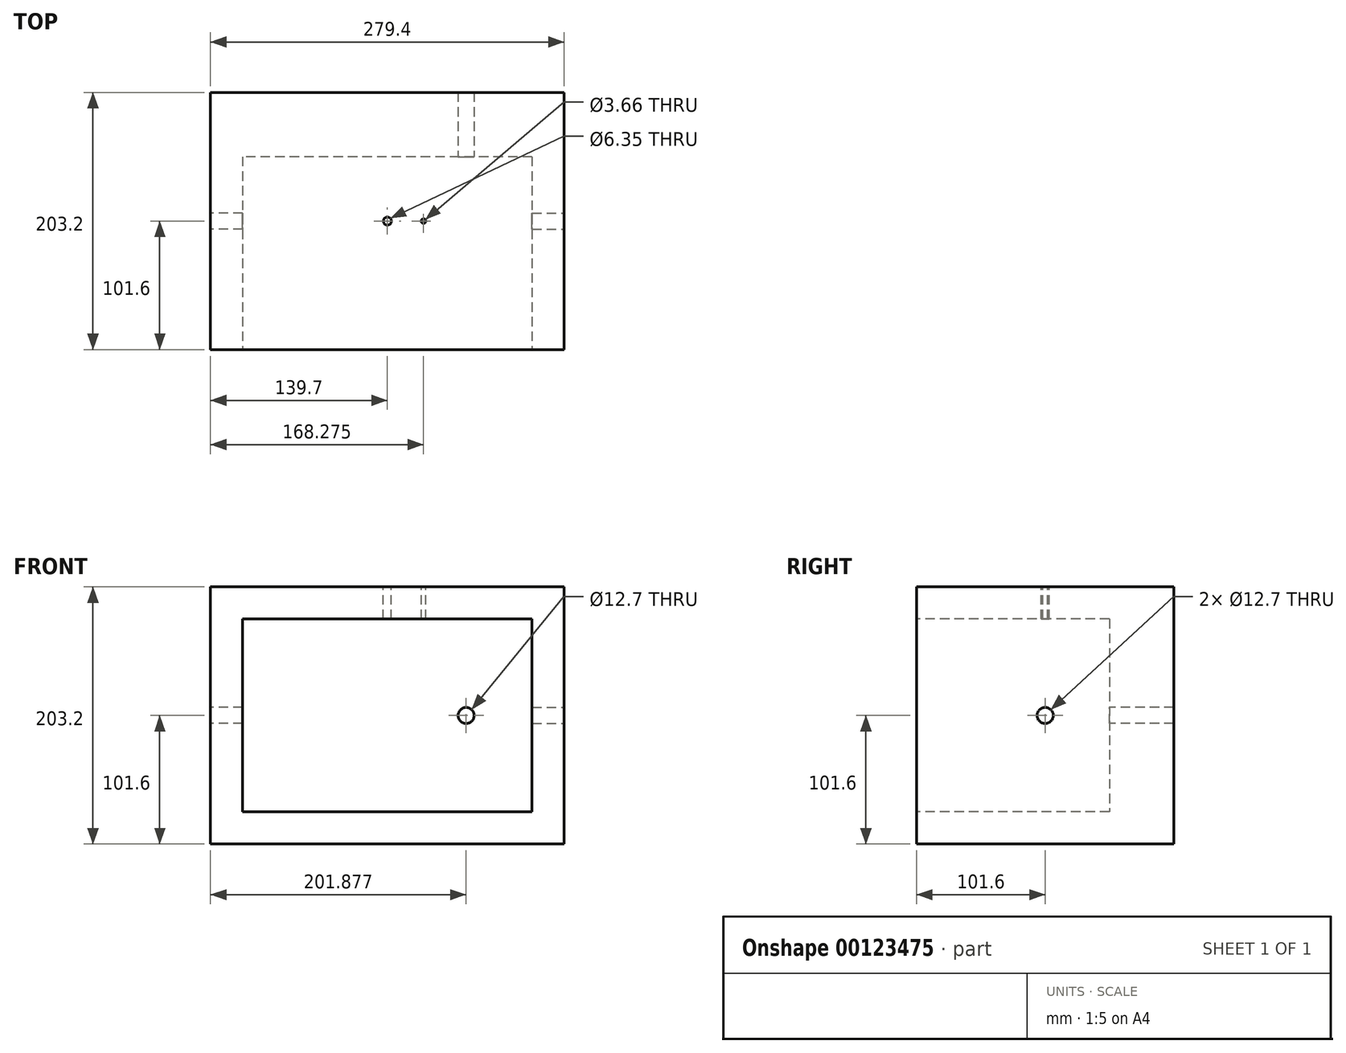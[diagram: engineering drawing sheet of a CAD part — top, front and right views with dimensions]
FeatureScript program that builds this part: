
annotation { "Feature Type Name" : "Feature", "Feature Type Description" : "" }
export const myFeature = defineFeature(function(context is Context, id is Id, definition is map)
    precondition{}
    {
        {
            var Q0;
            Q0=qCreatedBy(makeId("Front.planeOp"),FACE);
            var sketch = newSketch(context, id + "F0", { "sketchPlane" : qUnion([Q0])});
            skLineSegment(sketch, "E0.bottom", {"start": v(-139.7, 101.6) * mm, "end": v(139.7, 101.6) * mm});
            skLineSegment(sketch, "E0.top", {"start": v(-139.7, -101.6) * mm, "end": v(139.7, -101.6) * mm});
            skLineSegment(sketch, "E0.left", {"start": v(-139.7, 101.6) * mm, "end": v(-139.7, -101.6) * mm});
            skLineSegment(sketch, "E0.right", {"start": v(139.7, 101.6) * mm, "end": v(139.7, -101.6) * mm});
            skPoint(sketch, "E0.middle", {"position": v(0, 0) * mm});
            skSolve(sketch);
        }
        {
            var Q0;
            Q0=makeQuery(id+"F0.imprint","IMPRINT",FACE,{"disambiguationData":[TD([[makeQuery(id+"F0.imprint","IMPRINT",EDGE,{"derivedFrom":sQuery(id+"F0.wireOp",EDGE,"E0.bottom")}),-1.0]])]});
            extrude(context, id + "F1", {"entities" : qUnion([Q0]), "oppositeDirection" : true, "depth" : 203.2 * mm});
        }
        {
            var Q0;
            Q0=makeQuery(id+"F1.opExtrude","SWEPT_FACE",FACE,{"disambiguationData":[OSD([sQuery(id+"F0.wireOp",EDGE,"E0.bottom")])]});
            var sketch = newSketch(context, id + "F2", { "sketchPlane" : qUnion([Q0])});
            skCircle(sketch, "E1", {"center": v(0, 101.6) * mm, "radius": 3.18 * mm});
            skPoint(sketch, "E1.centerSnap0", {"position": v(139.7, 101.6) * mm});
            skLineSegment(sketch, "E2", {"start": v(0, 101.6) * mm, "end": v(28.58, 101.6) * mm, "construction": true});
            skCircle(sketch, "E3", {"center": v(28.58, 101.6) * mm, "radius": 1.83 * mm});
            skSolve(sketch);
        }
        {
            var Q0;
            Q0=makeQuery(id+"F1.opExtrude","SWEPT_FACE",FACE,{"disambiguationData":[OSD([sQuery(id+"F0.wireOp",EDGE,"E0.right")])]});
            var sketch = newSketch(context, id + "F3", { "sketchPlane" : qUnion([Q0])});
            skCircle(sketch, "E4", {"center": v(101.6, 0) * mm, "radius": 6.35 * mm});
            skPoint(sketch, "E4.centerSnap0", {"position": v(101.6, -101.6) * mm});
            skSolve(sketch);
        }
        {
            var Q0;
            Q0=makeQuery(id+"F1.opExtrude","SWEPT_FACE",FACE,{"disambiguationData":[OSD([sQuery(id+"F0.wireOp",EDGE,"E0.left")])]});
            var sketch = newSketch(context, id + "F4", { "sketchPlane" : qUnion([Q0])});
            skCircle(sketch, "E5", {"center": v(-101.6, 0) * mm, "radius": 6.35 * mm});
            skPoint(sketch, "E5.centerSnap0", {"position": v(-101.6, 101.6) * mm});
            skSolve(sketch);
        }
        {
            var Q0;
            Q0=qCreatedBy(makeId("Front.planeOp"),FACE);
            var sketch = newSketch(context, id + "F5", { "sketchPlane" : qUnion([Q0])});
            skLineSegment(sketch, "E6.bottom", {"start": v(114.3, 76.2) * mm, "end": v(-114.3, 76.2) * mm});
            skLineSegment(sketch, "E6.top", {"start": v(114.3, -76.2) * mm, "end": v(-114.3, -76.2) * mm});
            skLineSegment(sketch, "E6.left", {"start": v(114.3, 76.2) * mm, "end": v(114.3, -76.2) * mm});
            skLineSegment(sketch, "E6.right", {"start": v(-114.3, 76.2) * mm, "end": v(-114.3, -76.2) * mm});
            skSolve(sketch);
        }
        {
            var Q0;
            Q0=qSketchRegion(id+"F5",true);
            extrude(context, id + "F6", {"entities" : qUnion([Q0]), "operationType" : NewBodyOperationType.REMOVE, "oppositeDirection" : true, "depth" : 152.4 * mm});
        }
        {
            var Q0;
            Q0=makeQuery(id+"F2.imprint","IMPRINT",FACE,{"disambiguationData":[TD([[makeQuery(id+"F2.imprint","IMPRINT",EDGE,{"derivedFrom":sQuery(id+"F2.wireOp",EDGE,"E1")}),1.0]])]});
            var Q1;
            Q1=makeQuery(id+"F2.imprint","IMPRINT",FACE,{"disambiguationData":[TD([[makeQuery(id+"F2.imprint","IMPRINT",EDGE,{"derivedFrom":sQuery(id+"F2.wireOp",EDGE,"E3")}),1.0]])]});
            var Q2;
            Q2=sQuery(id+"F2.wireOp",EDGE,"E1");
            extrude(context, id + "F7", {"entities" : qUnion([Q0, Q1]), "operationType" : NewBodyOperationType.REMOVE, "surfaceEntities" : qUnion([Q2]), "oppositeDirection" : true, "depth" : 25.4 * mm});
        }
        {
            var Q0;
            Q0=qSketchRegion(id+"F3",true);
            extrude(context, id + "F8", {"entities" : qUnion([Q0]), "operationType" : NewBodyOperationType.REMOVE, "oppositeDirection" : true, "depth" : 25.4 * mm});
        }
        {
            var Q0;
            Q0=qSketchRegion(id+"F4",true);
            extrude(context, id + "F9", {"entities" : qUnion([Q0]), "operationType" : NewBodyOperationType.REMOVE, "oppositeDirection" : true, "depth" : 25.4 * mm});
        }
        {
            var Q0;
            Q0=qCreatedBy(makeId("Front.planeOp"),FACE);
            var sketch = newSketch(context, id + "F10", { "sketchPlane" : qUnion([Q0])});
            skCircle(sketch, "E7", {"center": v(62.18, 0) * mm, "radius": 6.35 * mm});
            skSolve(sketch);
        }
        {
            var Q0;
            Q0 = qSketchRegion(id + "F10", true);
            extrude(context, id + "F11", {"entities" : qUnion([Q0]), "operationType" : NewBodyOperationType.REMOVE, "oppositeDirection" : true, "depth" : 254 * mm});
        }
    });
